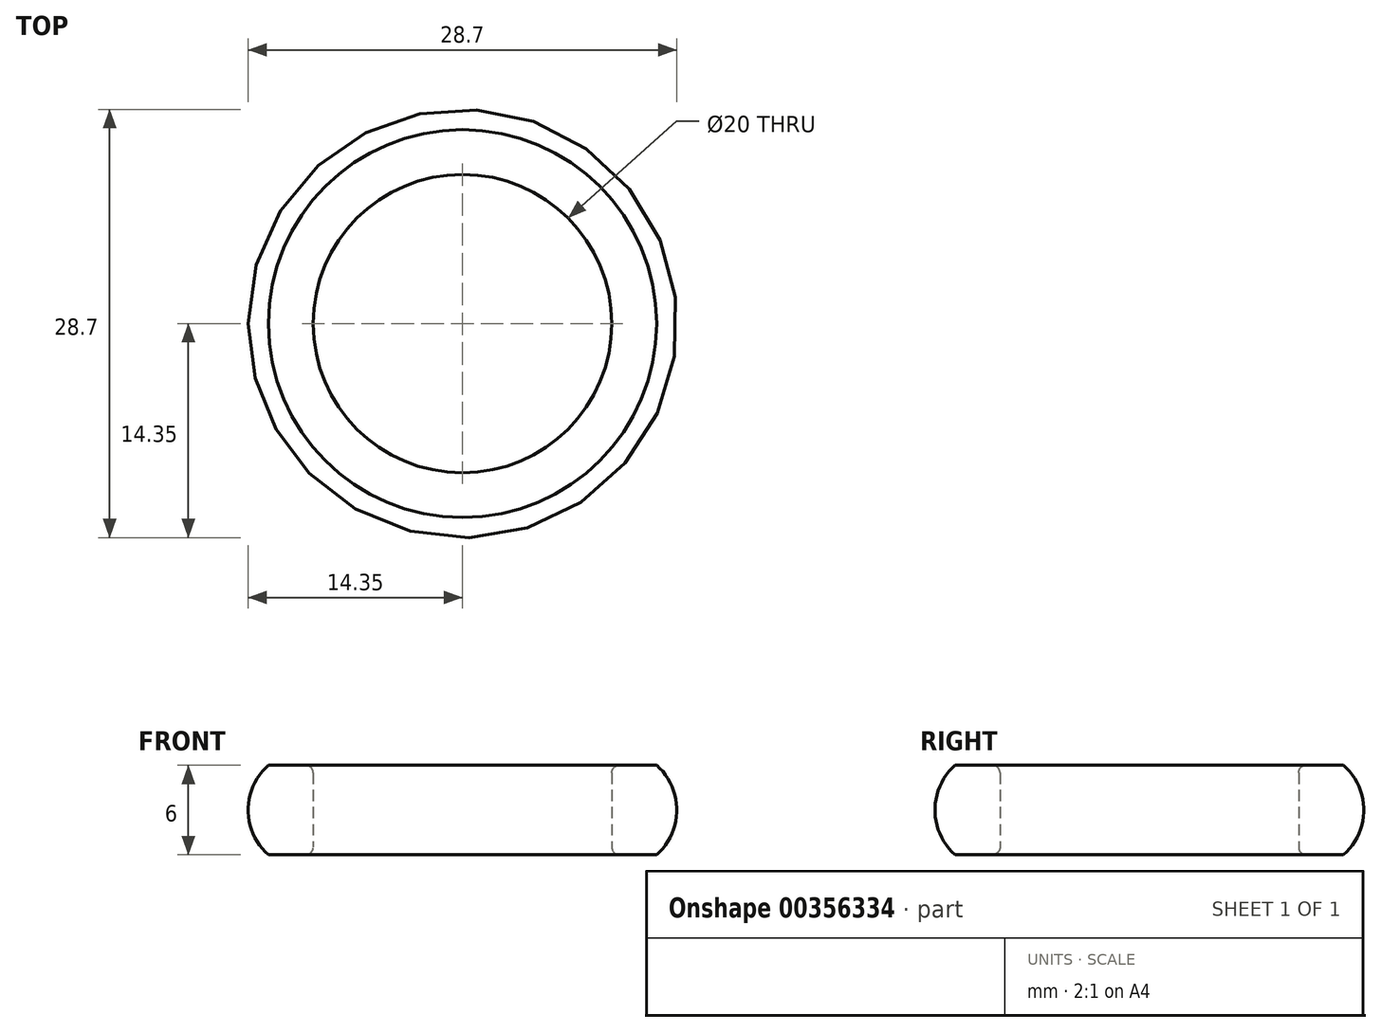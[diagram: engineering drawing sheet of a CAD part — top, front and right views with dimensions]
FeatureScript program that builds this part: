
annotation { "Feature Type Name" : "Feature", "Feature Type Description" : "" }
export const myFeature = defineFeature(function(context is Context, id is Id, definition is map)
    precondition{}
    {
        {
            var Q0;
            Q0=qCreatedBy(makeId("Front.planeOp"),FACE);
            var sketch = newSketch(context, id + "F0", { "sketchPlane" : qUnion([Q0])});
            skLineSegment(sketch, "E0", {"start": v(0, 0.5) * mm, "end": v(0, 5.5) * mm});
            skLineSegment(sketch, "E1", {"start": v(-0.5, 6) * mm, "end": v(-3, 6) * mm});
            skLineSegment(sketch, "E2", {"start": v(-0.5, 0) * mm, "end": v(-3, 0) * mm});
            skArc(sketch, "E3", {"start": v(-3, 6) * mm, "mid": v(-4.35, 3) * mm, "end": v(-3, 0) * mm});
            skPoint(sketch, "E4.visualSharp", {"position": v(0, 6) * mm});
            skArc(sketch, "E4.filletArc", {"start": v(0, 5.5) * mm, "mid": v(-0.15, 5.85) * mm, "end": v(-0.5, 6) * mm});
            skPoint(sketch, "E5.visualSharp", {"position": v(0, 0) * mm});
            skArc(sketch, "E5.filletArc", {"start": v(-0.5, 0) * mm, "mid": v(-0.15, 0.15) * mm, "end": v(0, 0.5) * mm});
            skLineSegment(sketch, "E6.0", {"start": v(10, 0.5) * mm, "end": v(10, 5.5) * mm});
            skSolve(sketch);
        }
        {
            var Q0;
            Q0=makeQuery(id+"F0.imprint","IMPRINT",FACE,{"disambiguationData":[TD([[makeQuery(id+"F0.imprint","IMPRINT",EDGE,{"derivedFrom":sQuery(id+"F0.wireOp",EDGE,"E0")}),1.0]])]});
            var Q1;
            Q1=sQuery(id+"F0.wireOp",EDGE,"E6.0");
            revolve(context, id + "F1", {"entities" : qUnion([Q0]), "axis" : qUnion([Q1]), "revolveType" : RevolveType.FULL});
        }
    });
